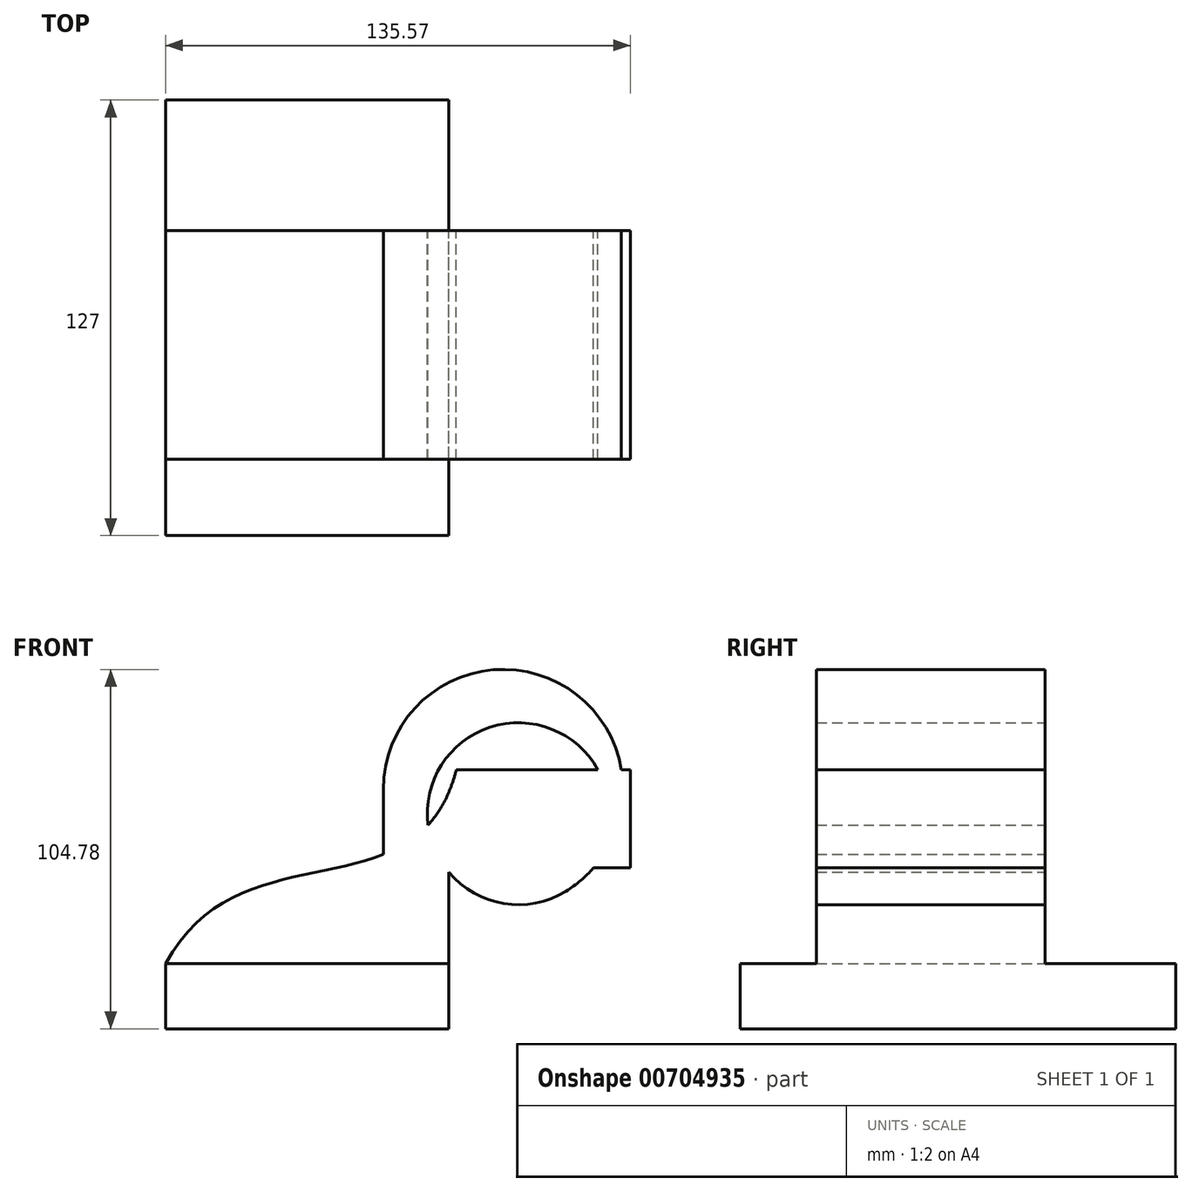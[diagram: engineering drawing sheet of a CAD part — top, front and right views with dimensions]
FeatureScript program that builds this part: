
annotation { "Feature Type Name" : "Feature", "Feature Type Description" : "" }
export const myFeature = defineFeature(function(context is Context, id is Id, definition is map)
    precondition{}
    {
        {
            var Q0;
            Q0=qCreatedBy(makeId("Front.planeOp"),FACE);
            var sketch = newSketch(context, id + "F0", { "sketchPlane" : qUnion([Q0])});
            skLineSegment(sketch, "E0.bottom", {"start": v(41.28, 9.53) * mm, "end": v(-41.28, 9.53) * mm});
            skLineSegment(sketch, "E0.top", {"start": v(41.28, -9.52) * mm, "end": v(-41.28, -9.52) * mm});
            skLineSegment(sketch, "E0.left", {"start": v(41.28, 9.53) * mm, "end": v(41.28, -9.52) * mm});
            skLineSegment(sketch, "E0.right", {"start": v(-41.28, 9.53) * mm, "end": v(-41.28, -9.52) * mm});
            skPoint(sketch, "E0.middle", {"position": v(0, 0) * mm});
            skLineSegment(sketch, "E1.bottom", {"start": v(94.29, 37.4) * mm, "end": v(43.49, 37.4) * mm});
            skLineSegment(sketch, "E1.top", {"start": v(94.29, 65.98) * mm, "end": v(43.49, 65.98) * mm});
            skLineSegment(sketch, "E1.left", {"start": v(94.29, 37.4) * mm, "end": v(94.29, 65.98) * mm});
            skLineSegment(sketch, "E1.right", {"start": v(43.49, 37.4) * mm, "end": v(43.49, 65.98) * mm});
            skPoint(sketch, "E1.middle", {"position": v(68.89, 51.69) * mm});
            skLineSegment(sketch, "E2", {"start": v(41.28, 9.53) * mm, "end": v(41.28, 60.33) * mm});
            skArc(sketch, "E3", {"start": v(41.27, 60.33) * mm, "mid": v(64.88, 74.19) * mm, "end": v(65.5, 46.82) * mm});
            skArc(sketch, "E4", {"start": v(65.5, 46.82) * mm, "mid": v(55.44, 57.45) * mm, "end": v(68.89, 51.69) * mm});
            skArc(sketch, "E5.0", {"start": v(75.5, 30.6) * mm, "mid": v(39.8, 68.35) * mm, "end": v(87.56, 47.9) * mm});
            skArc(sketch, "E5.1", {"start": v(22.23, 60.33) * mm, "mid": v(74.16, 90.83) * mm, "end": v(75.5, 30.6) * mm});
            skLineSegment(sketch, "E5.2", {"start": v(22.22, 9.53) * mm, "end": v(22.22, 60.33) * mm});
            skFitSpline(sketch, "E6", {"points": [v(-41.28, 9.52) * mm, v(43.49, 65.98) * mm], "startDerivative": vector(66.07, 122.14) * mm, "endDerivative": vector(33.11, 130.84) * mm});
            skSolve(sketch);
        }
        {
            var Q0;
            Q0=makeQuery(id+"F0.imprint","IMPRINT",FACE,{"disambiguationData":[TD([[makeQuery(id+"F0.imprint","IMPRINT",EDGE,{"derivedFrom":sQuery(id+"F0.wireOp",EDGE,"E0.top")}),-1.0]])]});
            extrude(context, id + "F1", {"entities" : qUnion([Q0]), "endBound" : BoundingType.SYMMETRIC, "depth" : 127 * mm, "offsetDistance" : 25.4 * mm});
        }
        {
            var Q0;
            Q0 = qSketchRegion(id + "F0", true);
            extrude(context, id + "F2", {"entities" : qUnion([Q0]), "operationType" : NewBodyOperationType.ADD, "endBound" : BoundingType.SYMMETRIC, "depth" : 50.8 * mm, "offsetDistance" : 25.4 * mm});
        }
        {
            var Q0;
            Q0 = qSketchRegion(id + "F0", true);
            var Q1;
            Q1=makeQuery(id+"F2.opExtrude","CAP_FACE",FACE,{"disambiguationData":[OSD([sQuery(id+"F0.wireOp",EDGE,"E0.top"),sQuery(id+"F0.wireOp",EDGE,"E0.left"),sQuery(id+"F0.wireOp",EDGE,"E0.right"),sQuery(id+"F0.wireOp",EDGE,"E1.bottom"),sQuery(id+"F0.wireOp",EDGE,"E1.top"),sQuery(id+"F0.wireOp",EDGE,"E1.left"),sQuery(id+"F0.wireOp",EDGE,"E2"),sQuery(id+"F0.wireOp",EDGE,"E5.0"),sQuery(id+"F0.wireOp",EDGE,"E5.1"),sQuery(id+"F0.wireOp",EDGE,"E5.2"),sQuery(id+"F0.wireOp",EDGE,"E6")])],"isStart":false});
            extrude(context, id + "F3", {"entities" : qUnion([Q0, Q1]), "operationType" : NewBodyOperationType.ADD, "depth" : 15.88 * mm, "offsetDistance" : 25.4 * mm});
        }
    });
